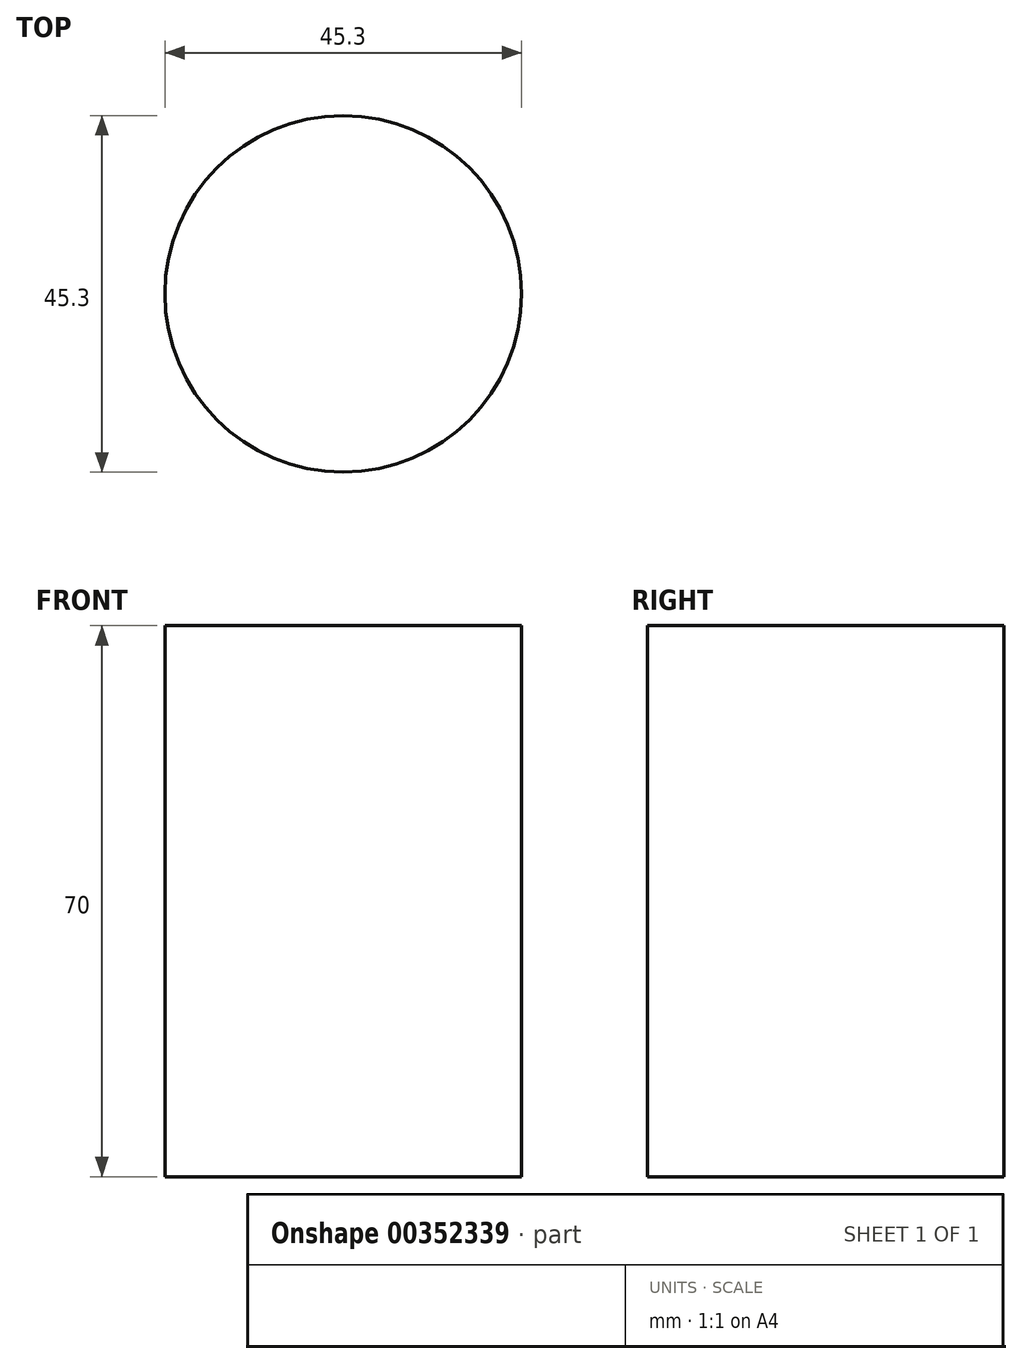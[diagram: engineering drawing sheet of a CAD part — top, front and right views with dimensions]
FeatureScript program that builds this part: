
annotation { "Feature Type Name" : "Feature", "Feature Type Description" : "" }
export const myFeature = defineFeature(function(context is Context, id is Id, definition is map)
    precondition{}
    {
        {
            var Q0;
            Q0=qCreatedBy(makeId("Top.planeOp"),FACE);
            var sketch = newSketch(context, id + "F0", { "sketchPlane" : qUnion([Q0])});
            skCircle(sketch, "E0", {"center": v(0, 0) * mm, "radius": 22.65 * mm});
            skSolve(sketch);
        }
        {
            var Q0;
            Q0=makeQuery(id+"F0.imprint","IMPRINT",FACE,{"disambiguationData":[TD([[makeQuery(id+"F0.imprint","IMPRINT",EDGE,{"derivedFrom":sQuery(id+"F0.wireOp",EDGE,"E0")}),1.0]])]});
            extrude(context, id + "F1", {"entities" : qUnion([Q0]), "depth" : 70 * mm});
        }
    });
